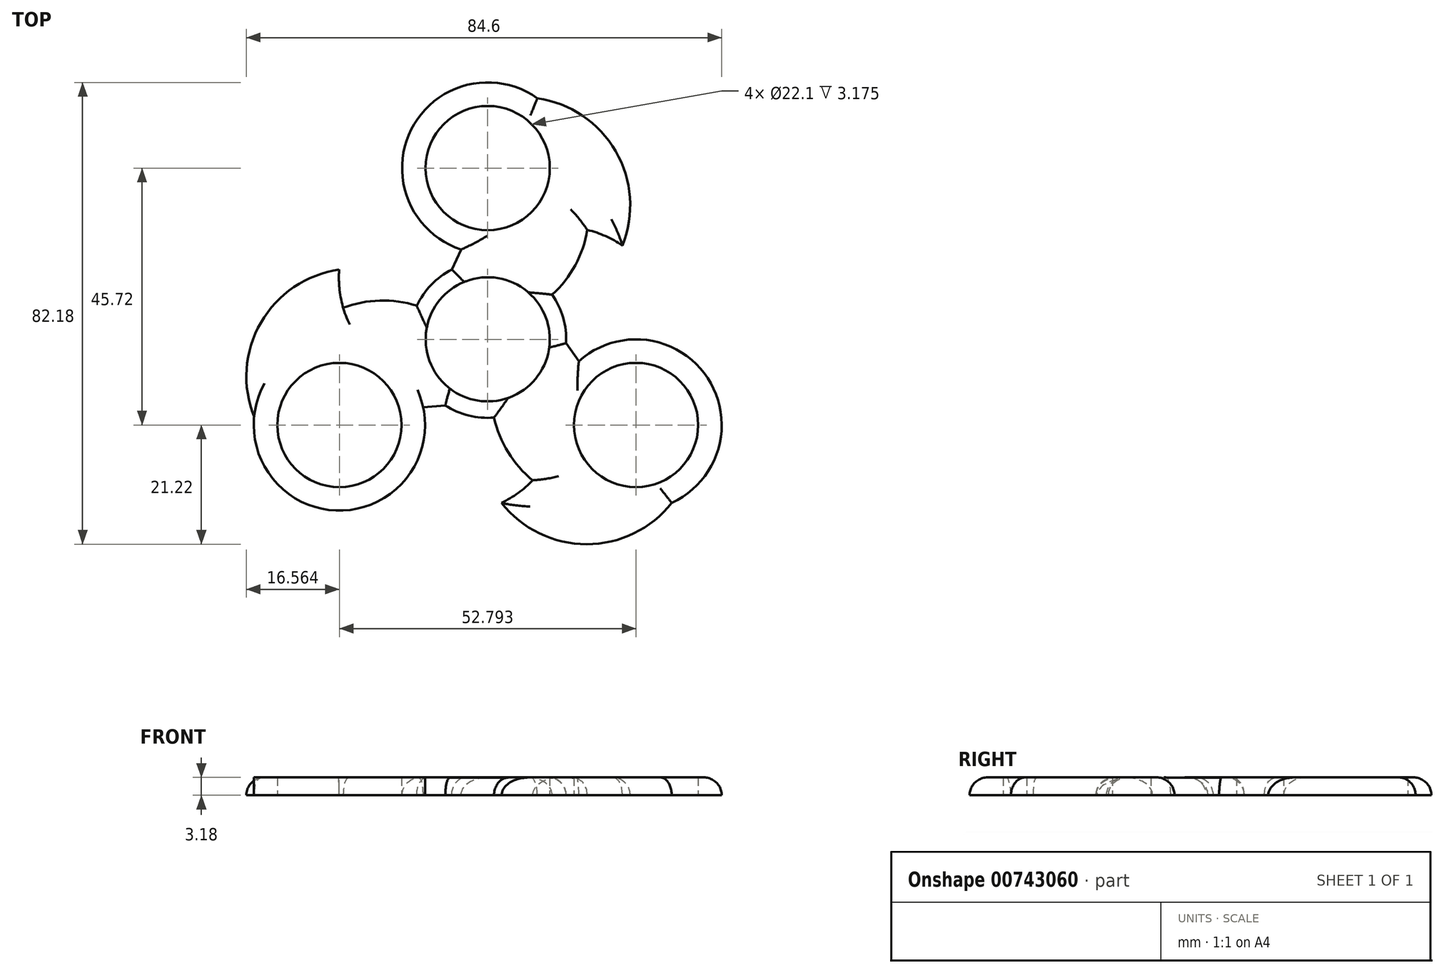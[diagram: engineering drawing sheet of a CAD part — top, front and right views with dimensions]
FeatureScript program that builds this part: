
annotation { "Feature Type Name" : "Feature", "Feature Type Description" : "" }
export const myFeature = defineFeature(function(context is Context, id is Id, definition is map)
    precondition{}
    {
        {
            var Q0;
            Q0=qCreatedBy(makeId("Top.planeOp"),FACE);
            var sketch = newSketch(context, id + "F0", { "sketchPlane" : qUnion([Q0])});
            skCircle(sketch, "E0", {"center": v(0, 0) * mm, "radius": 13.97 * mm});
            skCircle(sketch, "E1", {"center": v(0, 0) * mm, "radius": 11.05 * mm});
            skLineSegment(sketch, "E2", {"start": v(0, 0) * mm, "end": v(0, 30.48) * mm});
            skCircle(sketch, "E3", {"center": v(0, 30.48) * mm, "radius": 15.24 * mm});
            skCircle(sketch, "E4", {"center": v(0, 30.48) * mm, "radius": 11.05 * mm});
            skCircle(sketch, "E5.1.0", {"center": v(-26.4, -15.24) * mm, "radius": 11.05 * mm});
            skCircle(sketch, "E5.1.1", {"center": v(-26.4, -15.24) * mm, "radius": 15.24 * mm});
            skCircle(sketch, "E5.2.0", {"center": v(26.4, -15.24) * mm, "radius": 11.05 * mm});
            skCircle(sketch, "E5.2.1", {"center": v(26.4, -15.24) * mm, "radius": 15.24 * mm});
            skArc(sketch, "E6", {"start": v(14.61, -5.57) * mm, "mid": v(14.18, -4.56) * mm, "end": v(13.46, -3.73) * mm});
            skArc(sketch, "E7.1.0", {"start": v(-22.04, 4.97) * mm, "mid": v(-21.3, 1.54) * mm, "end": v(-19.68, -1.56) * mm});
            skPoint(sketch, "E8.orphan", {"position": v(21.84, -0.7) * mm});
            skPoint(sketch, "E9.orphan", {"position": v(15, 27.8) * mm});
            skPoint(sketch, "E10.orphan", {"position": v(16.58, -26.9) * mm});
            skPoint(sketch, "E11.orphan", {"position": v(-11.52, -18.56) * mm});
            skPoint(sketch, "E12.orphan", {"position": v(-10.32, 19.26) * mm});
            skPoint(sketch, "E13.orphan", {"position": v(-11.38, 8.1) * mm});
            skArc(sketch, "E14", {"start": v(11.5, 7.95) * mm, "mid": v(17.79, 19.92) * mm, "end": v(15, 33.16) * mm});
            skArc(sketch, "E15", {"start": v(32.1, 0) * mm, "mid": v(27.6, 13.43) * mm, "end": v(15, 19.92) * mm});
            skPoint(sketch, "E15.endSnap0", {"position": v(17.79, 19.92) * mm});
            skArc(sketch, "E16", {"start": v(23.96, 16.69) * mm, "mid": v(22.78, 33.47) * mm, "end": v(8.83, 42.9) * mm});
            skArc(sketch, "E17.1.0", {"start": v(-16.05, 27.8) * mm, "mid": v(-25.43, 17.18) * mm, "end": v(-24.75, 3.03) * mm});
            skArc(sketch, "E17.2.0", {"start": v(-16.05, -27.8) * mm, "mid": v(-2.17, -30.6) * mm, "end": v(9.75, -22.95) * mm});
            skArc(sketch, "E18.1.0", {"start": v(-26.43, 12.41) * mm, "mid": v(-40.38, 2.99) * mm, "end": v(-41.57, -13.8) * mm});
            skArc(sketch, "E18.1.1", {"start": v(-12.63, 5.98) * mm, "mid": v(-26.14, 5.45) * mm, "end": v(-36.22, -3.59) * mm});
            skArc(sketch, "E18.2.0", {"start": v(2.47, -29.1) * mm, "mid": v(17.6, -36.46) * mm, "end": v(32.74, -29.1) * mm});
            skArc(sketch, "E18.2.1", {"start": v(1.14, -13.92) * mm, "mid": v(8.36, -25.36) * mm, "end": v(21.21, -29.57) * mm});
            skLineSegment(sketch, "E19", {"start": v(-11.48, -12.1) * mm, "end": v(-7.55, -11.75) * mm});
            skLineSegment(sketch, "E20.1.0", {"start": v(16.22, -3.9) * mm, "end": v(13.95, -0.66) * mm});
            skLineSegment(sketch, "E20.2.0", {"start": v(-4.74, 16) * mm, "end": v(-6.4, 12.42) * mm});
            skSolve(sketch);
        }
        {
            var Q0;
            Q0 = qSketchRegion(id + "F0", true);
            extrude(context, id + "F1", {"entities" : qUnion([Q0]), "depth" : 3.17 * mm, "offsetDistance" : 25.4 * mm});
        }
        {
            var Q0;
            Q0 = qSketchRegion(id + "F0", true);
            extrude(context, id + "F2", {"entities" : qUnion([Q0]), "operationType" : NewBodyOperationType.ADD, "depth" : 3.17 * mm, "offsetDistance" : 25.4 * mm});
        }
        {
            var Q0;
            Q0=makeQuery(id+"F1.opExtrude","CAP_EDGE",EDGE,{"disambiguationData":[OSD([sQuery(id+"F0.wireOp",EDGE,"E16")])],"isStart":false});
            var Q1;
            Q1=makeQuery(id+"F1.opExtrude","CAP_EDGE",EDGE,{"disambiguationData":[OSD([sQuery(id+"F0.wireOp",EDGE,"E3")])],"isStart":false});
            var Q2;
            Q2=makeQuery(id+"F1.opExtrude","CAP_EDGE",EDGE,{"disambiguationData":[OSD([sQuery(id+"F0.wireOp",EDGE,"E14")])],"isStart":false});
            var Q3;
            {var subQ0=sQuery(id+"F0.wireOp",EDGE,"E0");Q3=makeQuery(id+"F1.opExtrude","CAP_EDGE",EDGE,{"disambiguationData":[OSD([subQ0]),TDD([makeQuery(id+"F0.imprint","IMPRINT",EDGE,{"disambiguationData":[TD([[makeQuery(id+"F0.imprint","INTERSECT",VERTEX,{"derivedFrom":[subQ0,sQuery(id+"F0.wireOp",EDGE,"E14")]}),1.0]])],"derivedFrom":subQ0})])],"isStart":false});}
            var Q4;
            Q4=makeQuery(id+"F1.opExtrude","CAP_EDGE",EDGE,{"disambiguationData":[OSD([sQuery(id+"F0.wireOp",EDGE,"E20.1.0")])],"isStart":false});
            var Q5;
            Q5=makeQuery(id+"F1.opExtrude","CAP_EDGE",EDGE,{"disambiguationData":[OSD([sQuery(id+"F0.wireOp",EDGE,"E5.2.1")])],"isStart":false});
            var Q6;
            Q6=makeQuery(id+"F1.opExtrude","CAP_EDGE",EDGE,{"disambiguationData":[OSD([sQuery(id+"F0.wireOp",EDGE,"E18.2.0")])],"isStart":false});
            var Q7;
            Q7=makeQuery(id+"F1.opExtrude","CAP_EDGE",EDGE,{"disambiguationData":[OSD([sQuery(id+"F0.wireOp",EDGE,"E17.2.0")])],"isStart":false});
            var Q8;
            Q8=makeQuery(id+"F1.opExtrude","CAP_EDGE",EDGE,{"disambiguationData":[OSD([sQuery(id+"F0.wireOp",EDGE,"E18.2.1")])],"isStart":false});
            var Q9;
            {var subQ0=sQuery(id+"F0.wireOp",EDGE,"E0");Q9=makeQuery(id+"F1.opExtrude","CAP_EDGE",EDGE,{"disambiguationData":[OSD([subQ0]),TDD([makeQuery(id+"F0.imprint","IMPRINT",EDGE,{"disambiguationData":[TD([[makeQuery(id+"F0.imprint","INTERSECT",VERTEX,{"derivedFrom":[subQ0,sQuery(id+"F0.wireOp",EDGE,"E18.2.1")]}),1.0]])],"derivedFrom":subQ0})])],"isStart":false});}
            var Q10;
            Q10=makeQuery(id+"F1.opExtrude","CAP_EDGE",EDGE,{"disambiguationData":[OSD([sQuery(id+"F0.wireOp",EDGE,"E19")])],"isStart":false});
            var Q11;
            Q11=makeQuery(id+"F1.opExtrude","CAP_EDGE",EDGE,{"disambiguationData":[OSD([sQuery(id+"F0.wireOp",EDGE,"E5.1.1")])],"isStart":false});
            var Q12;
            Q12=makeQuery(id+"F1.opExtrude","CAP_EDGE",EDGE,{"disambiguationData":[OSD([sQuery(id+"F0.wireOp",EDGE,"E18.1.0")])],"isStart":false});
            var Q13;
            Q13=makeQuery(id+"F1.opExtrude","CAP_EDGE",EDGE,{"disambiguationData":[OSD([sQuery(id+"F0.wireOp",EDGE,"E18.1.1")])],"isStart":false});
            var Q14;
            {var subQ0=sQuery(id+"F0.wireOp",EDGE,"E0");Q14=makeQuery(id+"F1.opExtrude","CAP_EDGE",EDGE,{"disambiguationData":[OSD([subQ0]),TDD([makeQuery(id+"F0.imprint","IMPRINT",EDGE,{"disambiguationData":[TD([[makeQuery(id+"F0.imprint","INTERSECT",VERTEX,{"derivedFrom":[subQ0,sQuery(id+"F0.wireOp",EDGE,"E18.1.1")]}),1.0]])],"derivedFrom":subQ0})])],"isStart":false});}
            var Q15;
            Q15=makeQuery(id+"F1.opExtrude","CAP_EDGE",EDGE,{"disambiguationData":[OSD([sQuery(id+"F0.wireOp",EDGE,"E20.2.0")])],"isStart":false});
            var Q16;
            Q16=makeQuery(id+"F1.opExtrude","CAP_EDGE",EDGE,{"disambiguationData":[OSD([sQuery(id+"F0.wireOp",EDGE,"E15")])],"isStart":false});
            fillet(context, id + "F3", {"entities" : qUnion([Q0, Q1, Q2, Q3, Q4, Q5, Q6, Q7, Q8, Q9, Q10, Q11, Q12, Q13, Q14, Q15, Q16]), "radius" : 3.17 * mm, "tangentPropagation" : true, "allowEdgeOverflow" : false});
        }
    });
